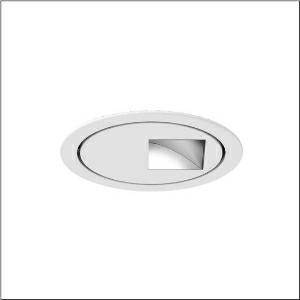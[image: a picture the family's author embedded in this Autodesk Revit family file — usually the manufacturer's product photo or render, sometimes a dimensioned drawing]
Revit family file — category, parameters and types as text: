
# Revit family: lunis_11_mini_round_51dk11cd2wm21
name_source: partatom
category: Lighting Fixtures
units: mm (PartAtom-declared; Revit-internal decimal feet)

## family parameters
Cut with Voids When Loaded = No
Host = Face
Light Source = No
Part Type = Normal
Room Calculation Point = No
Round Connector Dimension = Use Diameter
Shared = No

## types (1)
- Lunis 11 mini round (1 x LED 3000K / CRI = 90 (unbekannt), 1930 lm, 3000K)
    Apparent Load = 28 VA
    CIE Flux Codes = 44 77 97 100 100
    Color Rendering = 90
    Color Temperature = 3000K
    Default Elevation = 1800 mm
    Description = Lunis 11 mini round, downlight, light control with wallwasher, of highly reflective aluminium, highly specular, light emission: direct distribution, LED rated luminous flux: 1.930lm, light colour: 930, control gear: ECG, with terminal, 5-pole, mains connection: 220..230V, AC/DC, 0/50..60Hz, LED module, luminaire module, of aluminium, highly specular, white, diameter: 176mm, clamping range: 1..40mm, recessing ring, of plastic, traffic white (RAL 9016), protection rating (complete): IP20, insulation class (complete): insulation class II (safety insulation), certification: CE, permissible ambient temperature for indoor applications: 0..+35°C, packaging unit: 1 piece
    Height = 0 mm  [stored 0 ft]
    Lamp = 1 x LED 3000K / CRI >= 90 (unbekannt)
    Lamp Light Flux = 1930 lm
    Lamp count = 1
    Length = 176 mm
    Luminous efficacy = 69 lm/W
    Manufacturer = Siteco
    ModVariant = No
    Model = 51DK11CD2WM21
    Mounting Place = Ceiling
    Mounting Type = Recessed
    Number of Poles = 1
    OnlyDefault = Yes
    Power Factor = 1
    Product Name = Lunis 11 mini round
    Product group = downlight | ceiling recessed
    ProductGroupID = 402
    Protection Class = Protection class II
    Protection Degree = IP 20
    RLX_Detail_Level = 1
    RlxData = <blob elided: 59717 chars, md5=508bf043>
    Socket = socket
    Standby Power = 0 W
    System Light Flux = 1930 lm
    System Power = 28 W
    Type Comments = Product without accessories
    Type Image = l_1004772.jpg
    URL = http://relux.com
    VarID = ---
    Voltage = 0 V
    Weight = 0.00 kg
    Width = 176 mm

note: [stored X ft] marks values corroborated as IEEE doubles in the binary element streams (Revit-internal decimal feet)

## geometry (parser evidence)
native form markers: Blend x4, Sweep x10
no freeform markers — native parametric forms only
